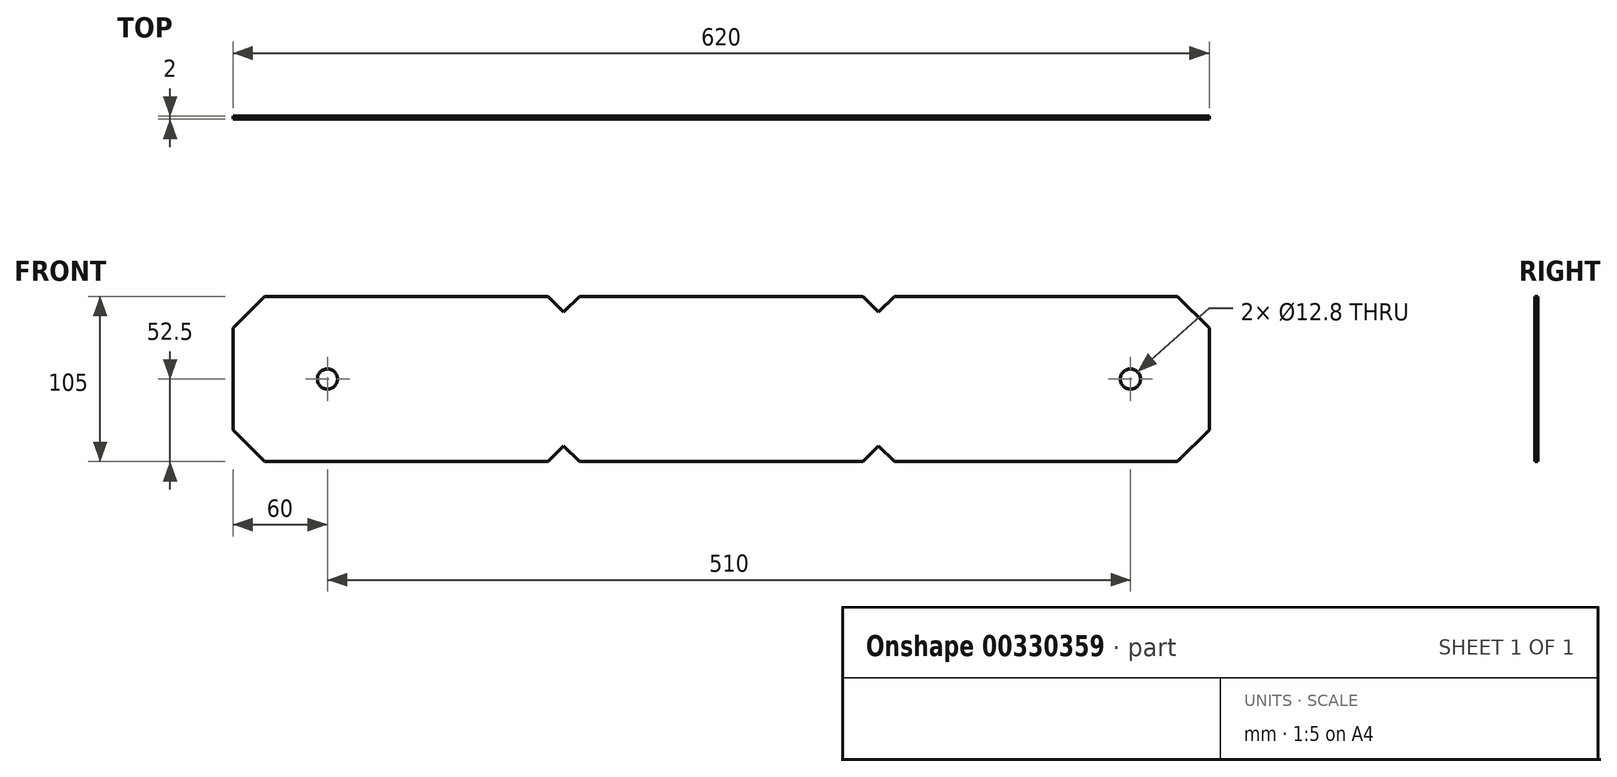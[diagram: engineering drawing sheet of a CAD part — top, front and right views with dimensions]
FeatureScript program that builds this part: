
annotation { "Feature Type Name" : "Feature", "Feature Type Description" : "" }
export const myFeature = defineFeature(function(context is Context, id is Id, definition is map)
    precondition{}
    {
        {
            var Q0;
            Q0=qCreatedBy(makeId("Front.planeOp"),FACE);
            var sketch = newSketch(context, id + "F0", { "sketchPlane" : qUnion([Q0])});
            skLineSegment(sketch, "E0.bottom", {"start": v(100, -42.5) * mm, "end": v(-100, -42.5) * mm});
            skLineSegment(sketch, "E0.top", {"start": v(100, 42.5) * mm, "end": v(-100, 42.5) * mm});
            skLineSegment(sketch, "E0.left", {"start": v(100, -42.5) * mm, "end": v(100, 42.5) * mm});
            skLineSegment(sketch, "E0.right", {"start": v(-100, -42.5) * mm, "end": v(-100, 42.5) * mm});
            skLineSegment(sketch, "E1.bottom", {"start": v(100, 42.5) * mm, "end": v(300, 42.5) * mm});
            skLineSegment(sketch, "E1.top", {"start": v(100, -42.5) * mm, "end": v(300, -42.5) * mm});
            skLineSegment(sketch, "E1.left", {"start": v(100, 42.5) * mm, "end": v(100, -42.5) * mm});
            skLineSegment(sketch, "E1.right", {"start": v(300, 42.5) * mm, "end": v(300, -42.5) * mm});
            skLineSegment(sketch, "E2.bottom", {"start": v(-100, 42.5) * mm, "end": v(-300, 42.5) * mm});
            skLineSegment(sketch, "E2.top", {"start": v(-100, -42.5) * mm, "end": v(-300, -42.5) * mm});
            skLineSegment(sketch, "E2.left", {"start": v(-100, 42.5) * mm, "end": v(-100, -42.5) * mm});
            skLineSegment(sketch, "E2.right", {"start": v(-300, 42.5) * mm, "end": v(-300, -42.5) * mm});
            skLineSegment(sketch, "E3", {"start": v(-300, 42.5) * mm, "end": v(-290, 52.5) * mm});
            skLineSegment(sketch, "E4", {"start": v(-100, 42.5) * mm, "end": v(-110, 52.5) * mm});
            skLineSegment(sketch, "E5", {"start": v(-290, 52.5) * mm, "end": v(-110, 52.5) * mm});
            skLineSegment(sketch, "E6", {"start": v(-100, 42.5) * mm, "end": v(-90, 52.5) * mm});
            skLineSegment(sketch, "E7", {"start": v(100, 42.5) * mm, "end": v(90, 52.5) * mm});
            skLineSegment(sketch, "E8", {"start": v(-90, 52.5) * mm, "end": v(90, 52.5) * mm});
            skLineSegment(sketch, "E9", {"start": v(-100, -42.5) * mm, "end": v(-110, -52.5) * mm});
            skLineSegment(sketch, "E10", {"start": v(-300, -42.5) * mm, "end": v(-290, -52.5) * mm});
            skLineSegment(sketch, "E11", {"start": v(-110, -52.5) * mm, "end": v(-290, -52.5) * mm});
            skLineSegment(sketch, "E12", {"start": v(100, -42.5) * mm, "end": v(90, -52.5) * mm});
            skLineSegment(sketch, "E13", {"start": v(-100, -42.5) * mm, "end": v(-90, -52.5) * mm});
            skLineSegment(sketch, "E14", {"start": v(90, -52.5) * mm, "end": v(-90, -52.5) * mm});
            skLineSegment(sketch, "E15", {"start": v(300, -42.5) * mm, "end": v(290, -52.5) * mm});
            skLineSegment(sketch, "E16", {"start": v(100, -42.5) * mm, "end": v(110, -52.5) * mm});
            skLineSegment(sketch, "E17", {"start": v(290, -52.5) * mm, "end": v(110, -52.5) * mm});
            skLineSegment(sketch, "E18", {"start": v(100, 42.5) * mm, "end": v(110, 52.5) * mm});
            skLineSegment(sketch, "E19", {"start": v(300, 42.5) * mm, "end": v(290, 52.5) * mm});
            skLineSegment(sketch, "E20", {"start": v(110, 52.5) * mm, "end": v(290, 52.5) * mm});
            skLineSegment(sketch, "E21", {"start": v(300, 42.5) * mm, "end": v(310, 32.5) * mm});
            skLineSegment(sketch, "E22", {"start": v(310, 32.5) * mm, "end": v(310, -32.5) * mm});
            skLineSegment(sketch, "E23", {"start": v(310, -32.5) * mm, "end": v(300, -42.5) * mm});
            skLineSegment(sketch, "E24", {"start": v(-300, -42.5) * mm, "end": v(-310, -32.5) * mm});
            skLineSegment(sketch, "E25", {"start": v(-310, -32.5) * mm, "end": v(-310, 32.5) * mm});
            skLineSegment(sketch, "E26", {"start": v(-310, 32.5) * mm, "end": v(-300, 42.5) * mm});
            skCircle(sketch, "E27", {"center": v(-250, 0) * mm, "radius": 6.4 * mm});
            skCircle(sketch, "E28", {"center": v(260, 0) * mm, "radius": 6.4 * mm});
            skSolve(sketch);
        }
        {
            var Q0;
            Q0 = qSketchRegion(id + "F0", true);
            extrude(context, id + "F1", {"entities" : qUnion([Q0]), "depth" : 2 * mm});
        }
    });
